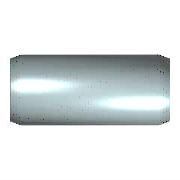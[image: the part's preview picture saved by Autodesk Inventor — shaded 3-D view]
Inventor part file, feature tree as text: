
AUTODESK INVENTOR PART (.ipt)
format: ipt  version: 2023.3 (Build 273359000, 359)  size: 163,328 bytes
history: native  units: mm (DEFAULTED — no unit token found)
features: sketch x5, extrude x3, plane x2, chamfer x1, hole x1, revolve x1
ambient origin geometry x8: Origin, YZ Plane, XZ Plane, XY Plane, X Axis, Y Axis, Z Axis, Center Point
bodies: Solid1 (feature_tree)
feature tree (13):
  extrude  "Körper"  Depth=3.0mm TaperAngle=0.0deg
  chamfer  "Skizze2"  Distance=0.5mm
  plane  "Arbeitsebene1"
  hole  "Bohrung1"  [1 undecoded]
  extrude  "Extrusion2"  TaperAngle=0.0deg  [1 undecoded]
  plane  "Arbeitsebene2"
  extrude  "Extrusion3"  TaperAngle=0.0deg  [1 undecoded]
  revolve  "Umdrehung1"
  sketch  "Skizze"  dims[d9=15.0deg d11=0.5mm d12=0.5mm d13=0.0mm d15=0.0mm d16=0.0mm d17=1.5mm d18=6.0mm d19=0.5mm d20=6.0mm d21=1.7mm d22=2.0mm d23=30.0deg d24=12.0mm d25=0.0mm d26=2.0mm d27=6.0mm d28=1.0mm d29=0.0mm d30=0.0mm d31=-1.5mm d32=3.0mm d33=5.0mm d34=0.5mm d35=0.0mm d36=1.0mm d37=1.0mm d38=0.75mm d39=90.0deg]
  sketch  "Skizze3"  dims[d1=3.0mm d2=16.0mm d3=0.0mm]
  sketch  "Skizze4"  dims[d4=0.5mm]
  sketch  "Skizze5"  dims[d5=15.0deg]
  sketch  "Skizze6"  dims[d8=0.5mm]
note: 3 required parameter values undecoded (feature->parameter linkage not recoverable at this tier; creation-order binding heuristic only, values carry confidence <= 0.55)
